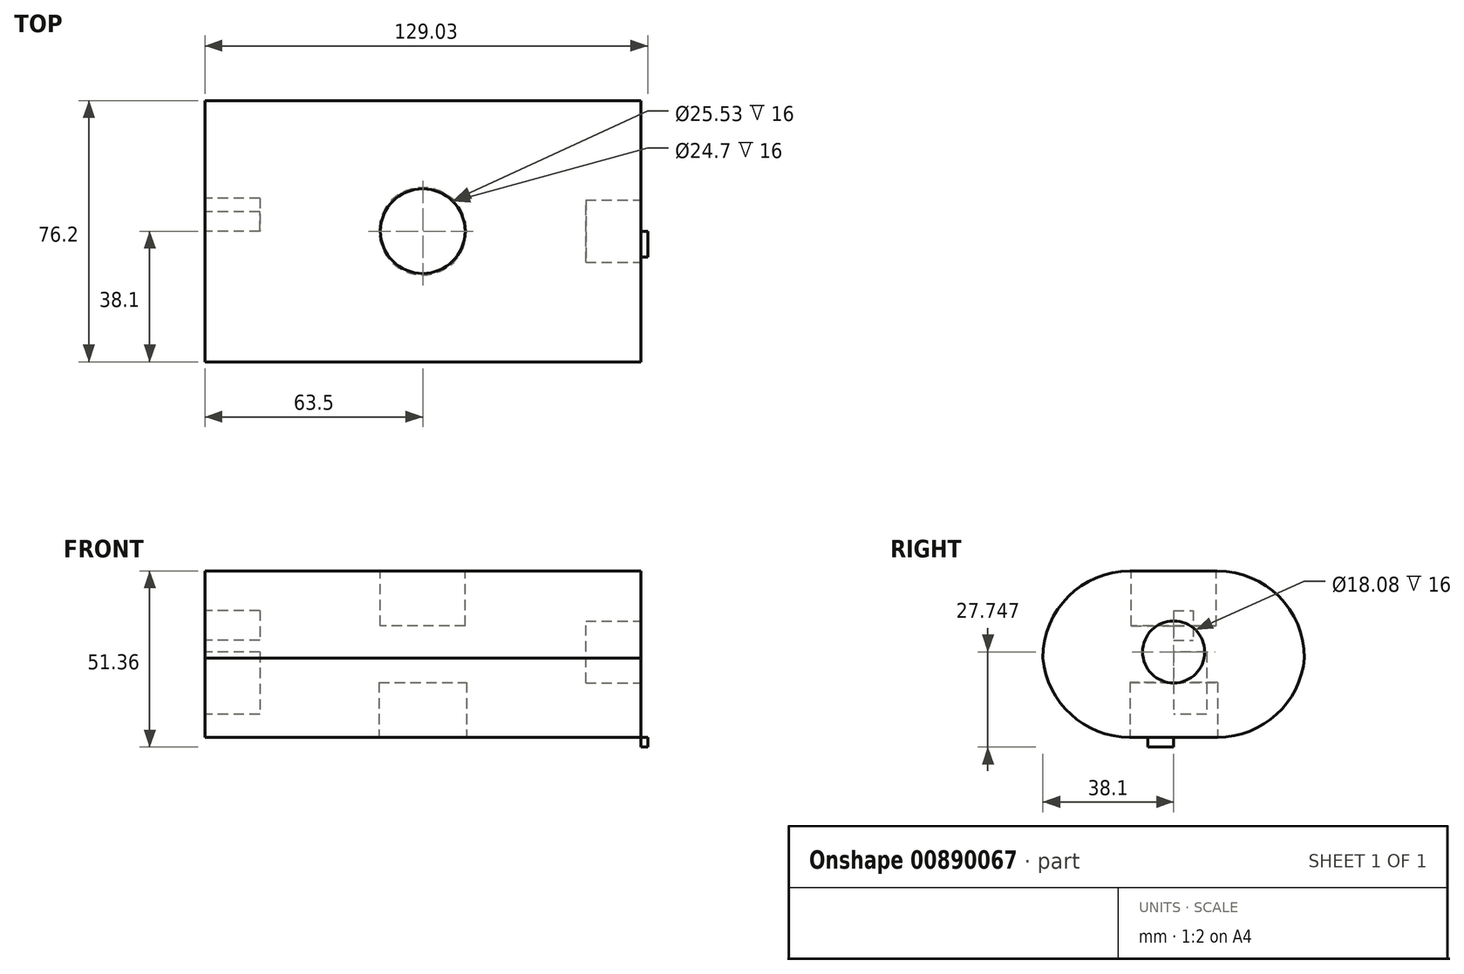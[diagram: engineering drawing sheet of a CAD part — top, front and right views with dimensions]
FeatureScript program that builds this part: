
annotation { "Feature Type Name" : "Feature", "Feature Type Description" : "" }
export const myFeature = defineFeature(function(context is Context, id is Id, definition is map)
    precondition{}
    {
        {
            var Q0;
            Q0=qCreatedBy(makeId("Top.planeOp"),FACE);
            var sketch = newSketch(context, id + "F0", { "sketchPlane" : qUnion([Q0])});
            skLineSegment(sketch, "E0.bottom", {"start": v(-63.5, -38.1) * mm, "end": v(63.5, -38.1) * mm});
            skLineSegment(sketch, "E0.top", {"start": v(-63.5, 38.1) * mm, "end": v(63.5, 38.1) * mm});
            skLineSegment(sketch, "E0.left", {"start": v(-63.5, -38.1) * mm, "end": v(-63.5, 38.1) * mm});
            skLineSegment(sketch, "E0.right", {"start": v(63.5, -38.1) * mm, "end": v(63.5, 38.1) * mm});
            skPoint(sketch, "E0.middle", {"position": v(0, 0) * mm});
            skSolve(sketch);
        }
        {
            var Q0;
            Q0 = qSketchRegion(id + "F0", true);
            extrude(context, id + "F1", {"entities" : qUnion([Q0]), "depth" : 48.5 * mm, "offsetDistance" : 25.4 * mm});
        }
        {
            var Q0;
            Q0=makeQuery(id+"F1.opExtrude","CAP_EDGE",EDGE,{"disambiguationData":[OSD([sQuery(id+"F0.wireOp",EDGE,"E0.bottom")])],"isStart":false});
            fillet(context, id + "F2", {"entities" : qUnion([Q0]), "radius" : 25.4 * mm, "tangentPropagation" : true, "allowEdgeOverflow" : false});
        }
        {
            var Q0;
            Q0=makeQuery(id+"F1.opExtrude","CAP_EDGE",EDGE,{"disambiguationData":[OSD([sQuery(id+"F0.wireOp",EDGE,"E0.bottom")])],"isStart":true});
            var Q1;
            Q1=makeQuery(id+"F1.opExtrude","CAP_EDGE",EDGE,{"disambiguationData":[OSD([sQuery(id+"F0.wireOp",EDGE,"E0.top")])],"isStart":false});
            fillet(context, id + "F3", {"entities" : qUnion([Q0, Q1]), "radius" : 25.4 * mm, "tangentPropagation" : true, "allowEdgeOverflow" : false});
        }
        {
            var Q0;
            Q0=makeQuery(id+"F1.opExtrude","CAP_EDGE",EDGE,{"disambiguationData":[OSD([sQuery(id+"F0.wireOp",EDGE,"E0.top")])],"isStart":true});
            fillet(context, id + "F4", {"entities" : qUnion([Q0]), "radius" : 25.4 * mm, "tangentPropagation" : true, "allowEdgeOverflow" : false});
        }
        {
            var Q0;
            Q0=makeQuery(id+"F1.opExtrude","SWEPT_FACE",FACE,{"disambiguationData":[OSD([sQuery(id+"F0.wireOp",EDGE,"E0.right")])]});
            var sketch = newSketch(context, id + "F5", { "sketchPlane" : qUnion([Q0])});
            skPoint(sketch, "E1.firstSnap0", {"position": v(0, 0) * mm});
            skLineSegment(sketch, "E1.bottom", {"start": v(0, -2.85) * mm, "end": v(-7.5, -2.85) * mm});
            skLineSegment(sketch, "E1.top", {"start": v(0, 9.9) * mm, "end": v(-7.5, 9.9) * mm});
            skLineSegment(sketch, "E1.left", {"start": v(0, -2.85) * mm, "end": v(0, 9.9) * mm});
            skLineSegment(sketch, "E1.right", {"start": v(-7.5, -2.85) * mm, "end": v(-7.5, 9.9) * mm});
            skSolve(sketch);
        }
        {
            var Q0;
            {var subQ0=sQuery(id+"F5.wireOp",EDGE,"E1.bottom");Q0=makeQuery(id+"F5.imprint","IMPRINT",FACE,{"disambiguationData":[TD([[makeQuery(id+"F5.imprint","IMPRINT",EDGE,{"derivedFrom":subQ0}),-1.0]])]});}
            var Q1;
            Q1=makeQuery(id+"F1.opExtrude","SWEPT_FACE",FACE,{"disambiguationData":[OSD([sQuery(id+"F0.wireOp",EDGE,"E0.left")])]});
            extrude(context, id + "F6", {"entities" : qUnion([Q0, Q1]), "operationType" : NewBodyOperationType.ADD, "depth" : 2.03 * mm, "offsetDistance" : 25.4 * mm});
        }
        {
            var Q0;
            Q0=makeQuery(id+"F1.opExtrude","SWEPT_FACE",FACE,{"disambiguationData":[OSD([sQuery(id+"F0.wireOp",EDGE,"E0.left")])]});
            var sketch = newSketch(context, id + "F7", { "sketchPlane" : qUnion([Q0])});
            skLineSegment(sketch, "E2", {"start": v(-9.65, 24.86) * mm, "end": v(-9.65, 6.72) * mm});
            skLineSegment(sketch, "E3", {"start": v(-9.65, 24.86) * mm, "end": v(0, 24.86) * mm});
            skLineSegment(sketch, "E4", {"start": v(-9.65, 6.72) * mm, "end": v(0, 6.72) * mm});
            skLineSegment(sketch, "E5", {"start": v(0, 24.86) * mm, "end": v(0, 6.72) * mm});
            skSolve(sketch);
        }
        {
            var Q0;
            Q0=makeQuery(id+"F7.imprint","IMPRINT",FACE,{"disambiguationData":[TD([[makeQuery(id+"F7.imprint","IMPRINT",EDGE,{"derivedFrom":sQuery(id+"F7.wireOp",EDGE,"E2")}),1.0]])]});
            extrude(context, id + "F8", {"entities" : qUnion([Q0]), "operationType" : NewBodyOperationType.REMOVE, "oppositeDirection" : true, "depth" : 16 * mm, "offsetDistance" : 25.4 * mm});
        }
        {
            var Q0;
            Q0=makeQuery(id+"F1.opExtrude","SWEPT_FACE",FACE,{"disambiguationData":[OSD([sQuery(id+"F0.wireOp",EDGE,"E0.left")])]});
            var sketch = newSketch(context, id + "F9", { "sketchPlane" : qUnion([Q0])});
            skLineSegment(sketch, "E6.bottom", {"start": v(0, 36.96) * mm, "end": v(-5.62, 36.96) * mm});
            skLineSegment(sketch, "E6.top", {"start": v(0, 28.32) * mm, "end": v(-5.62, 28.32) * mm});
            skLineSegment(sketch, "E6.left", {"start": v(0, 36.96) * mm, "end": v(0, 28.32) * mm});
            skLineSegment(sketch, "E6.right", {"start": v(-5.62, 36.96) * mm, "end": v(-5.62, 28.32) * mm});
            skSolve(sketch);
        }
        {
            var Q0;
            Q0 = qSketchRegion(id + "F9", true);
            extrude(context, id + "F10", {"entities" : qUnion([Q0]), "operationType" : NewBodyOperationType.REMOVE, "oppositeDirection" : true, "depth" : 16 * mm, "offsetDistance" : 25.4 * mm});
        }
        {
            var Q0;
            Q0=makeQuery(id+"F1.opExtrude","SWEPT_FACE",FACE,{"disambiguationData":[OSD([sQuery(id+"F0.wireOp",EDGE,"E0.right")])]});
            var sketch = newSketch(context, id + "F11", { "sketchPlane" : qUnion([Q0])});
            skCircle(sketch, "E7", {"center": v(0, 24.9) * mm, "radius": 9.04 * mm});
            skSolve(sketch);
        }
        {
            var Q0;
            Q0 = qSketchRegion(id + "F11", true);
            extrude(context, id + "F12", {"entities" : qUnion([Q0]), "operationType" : NewBodyOperationType.REMOVE, "oppositeDirection" : true, "depth" : 16 * mm, "offsetDistance" : 25.4 * mm});
        }
        {
            var Q0;
            Q0=makeQuery(id+"F1.opExtrude","CAP_FACE",FACE,{"disambiguationData":[OSD([sQuery(id+"F0.wireOp",EDGE,"E0.bottom"),sQuery(id+"F0.wireOp",EDGE,"E0.top"),sQuery(id+"F0.wireOp",EDGE,"E0.left"),sQuery(id+"F0.wireOp",EDGE,"E0.right")])],"isStart":true});
            var sketch = newSketch(context, id + "F13", { "sketchPlane" : qUnion([Q0])});
            skCircle(sketch, "E8", {"center": v(0, 0) * mm, "radius": 12.76 * mm});
            skSolve(sketch);
        }
        {
            var Q0;
            Q0 = qSketchRegion(id + "F13", true);
            extrude(context, id + "F14", {"entities" : qUnion([Q0]), "operationType" : NewBodyOperationType.REMOVE, "oppositeDirection" : true, "depth" : 16 * mm, "offsetDistance" : 25.4 * mm});
        }
        {
            var Q0;
            Q0=makeQuery(id+"F1.opExtrude","CAP_FACE",FACE,{"disambiguationData":[OSD([sQuery(id+"F0.wireOp",EDGE,"E0.bottom"),sQuery(id+"F0.wireOp",EDGE,"E0.top"),sQuery(id+"F0.wireOp",EDGE,"E0.left"),sQuery(id+"F0.wireOp",EDGE,"E0.right")])],"isStart":false});
            var sketch = newSketch(context, id + "F15", { "sketchPlane" : qUnion([Q0])});
            skCircle(sketch, "E9", {"center": v(0, 0) * mm, "radius": 12.35 * mm});
            skSolve(sketch);
        }
        {
            var Q0;
            Q0 = qSketchRegion(id + "F15", true);
            extrude(context, id + "F16", {"entities" : qUnion([Q0]), "operationType" : NewBodyOperationType.REMOVE, "oppositeDirection" : true, "depth" : 16 * mm, "offsetDistance" : 25.4 * mm});
        }
        {
            var Q0;
            Q0=makeQuery(id+"F1.opExtrude","CAP_FACE",FACE,{"disambiguationData":[OSD([sQuery(id+"F0.wireOp",EDGE,"E0.bottom"),sQuery(id+"F0.wireOp",EDGE,"E0.top"),sQuery(id+"F0.wireOp",EDGE,"E0.left"),sQuery(id+"F0.wireOp",EDGE,"E0.right")])],"isStart":false});
            var sketch = newSketch(context, id + "F17", { "sketchPlane" : qUnion([Q0])});
            skCircle(sketch, "E10", {"center": v(-48.04, 0) * mm, "radius": 4.96 * mm});
            skSolve(sketch);
        }
        {
            var Q0;
            Q0 = qSketchRegion(id + "F17", true);
            extrude(context, id + "F18", {"entities" : qUnion([Q0]), "operationType" : NewBodyOperationType.ADD, "oppositeDirection" : true, "depth" : 1 * mm, "offsetDistance" : 25.4 * mm});
        }
    });
